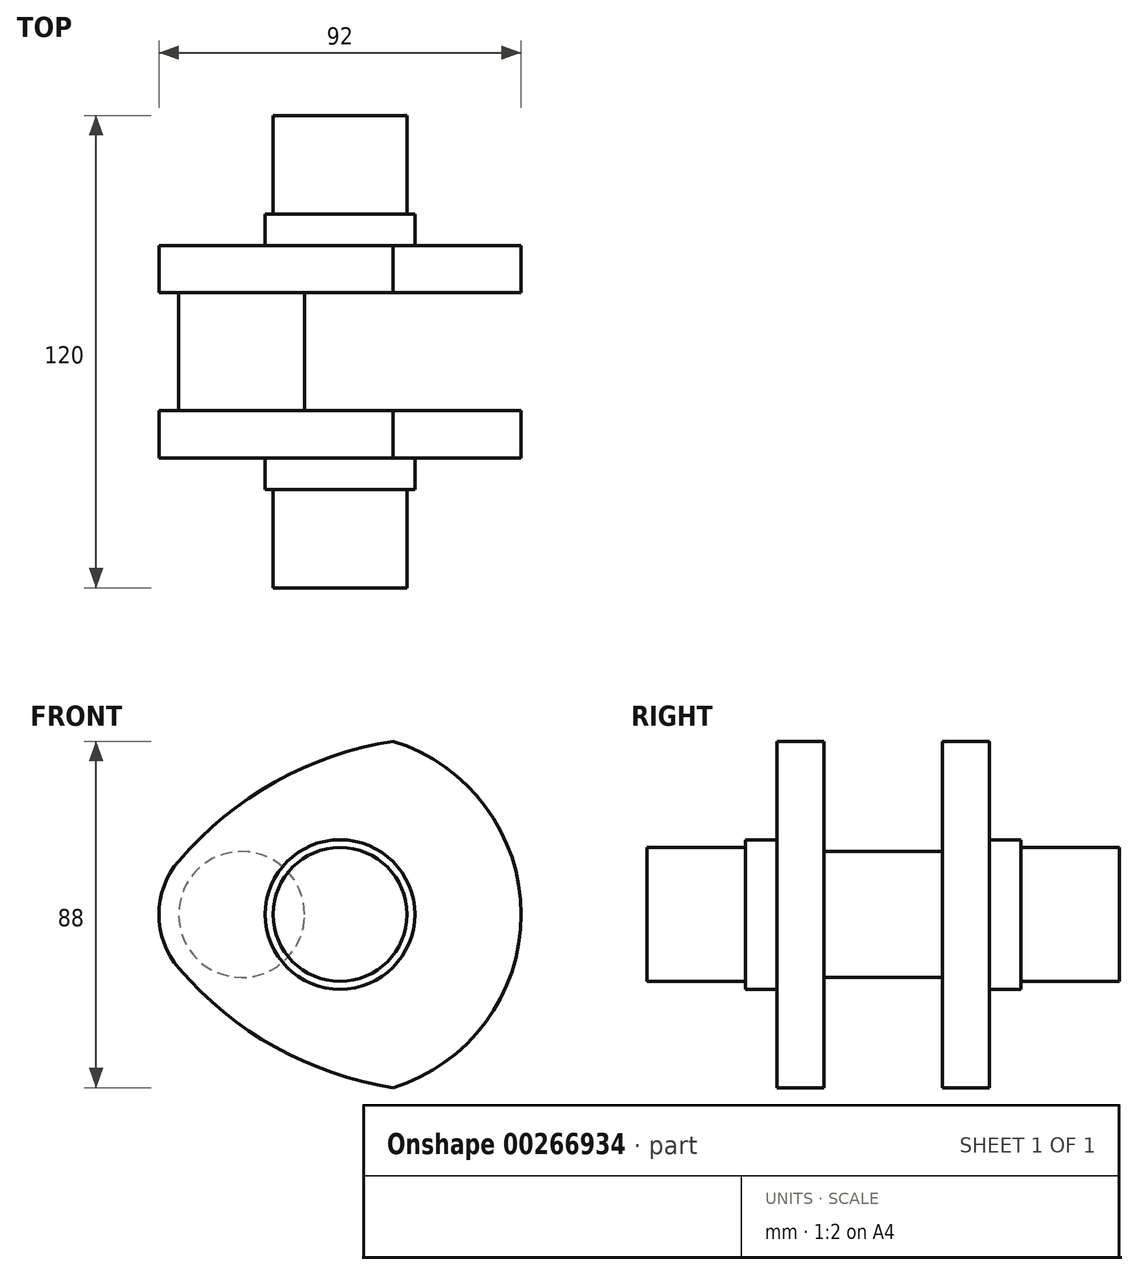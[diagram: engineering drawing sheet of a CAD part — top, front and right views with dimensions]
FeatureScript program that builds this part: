
annotation { "Feature Type Name" : "Feature", "Feature Type Description" : "" }
export const myFeature = defineFeature(function(context is Context, id is Id, definition is map)
    precondition{}
    {
        {
            var Q0;
            Q0=qCreatedBy(makeId("Front.planeOp"),FACE);
            var sketch = newSketch(context, id + "F0", { "sketchPlane" : qUnion([Q0])});
            skCircle(sketch, "E0", {"center": v(0, 0) * mm, "radius": 17 * mm});
            skSolve(sketch);
        }
        {
            var Q0;
            Q0=makeQuery(id+"F0.imprint","IMPRINT",FACE,{"disambiguationData":[TD([[makeQuery(id+"F0.imprint","IMPRINT",EDGE,{"derivedFrom":sQuery(id+"F0.wireOp",EDGE,"E0")}),1.0]])]});
            extrude(context, id + "F1", {"entities" : qUnion([Q0]), "depth" : 25 * mm});
        }
        {
            var Q0;
            Q0=makeQuery(id+"F0.imprint","IMPRINT",FACE,{"disambiguationData":[TD([[makeQuery(id+"F0.imprint","IMPRINT",EDGE,{"derivedFrom":sQuery(id+"F0.wireOp",EDGE,"E0")}),1.0]])]});
            var sketch = newSketch(context, id + "F2", { "sketchPlane" : qUnion([Q0])});
            skCircle(sketch, "E1", {"center": v(0, 0) * mm, "radius": 19 * mm});
            skSolve(sketch);
        }
        {
            var Q0;
            Q0 = qSketchRegion(id + "F2", true);
            extrude(context, id + "F3", {"entities" : qUnion([Q0]), "operationType" : NewBodyOperationType.ADD, "oppositeDirection" : true, "depth" : 8 * mm});
        }
        {
            var Q0;
            Q0=makeQuery(id+"F3.opExtrude","CAP_FACE",FACE,{"disambiguationData":[OSD([sQuery(id+"F2.wireOp",EDGE,"E1")])],"isStart":false});
            var sketch = newSketch(context, id + "F4", { "sketchPlane" : qUnion([Q0])});
            skArc(sketch, "E2", {"start": v(-13.42, 44) * mm, "mid": v(-46, 0) * mm, "end": v(-13.42, -44) * mm});
            skArc(sketch, "E3", {"start": v(40.94, -13.67) * mm, "mid": v(46, 0) * mm, "end": v(40.94, 13.67) * mm});
            skLineSegment(sketch, "E4", {"start": v(58.32, 0) * mm, "end": v(-25.77, 0) * mm, "construction": true});
            skArc(sketch, "E5", {"start": v(40.94, 13.67) * mm, "mid": v(16.47, 33.68) * mm, "end": v(-13.42, 44) * mm});
            skArc(sketch, "E6", {"start": v(-13.42, -44) * mm, "mid": v(16.47, -33.68) * mm, "end": v(40.94, -13.67) * mm});
            skSolve(sketch);
        }
        {
            var Q0;
            Q0=makeQuery(id+"F4.imprint","IMPRINT",FACE,{"disambiguationData":[TD([[makeQuery(id+"F4.imprint","IMPRINT",EDGE,{"derivedFrom":sQuery(id+"F4.wireOp",EDGE,"E2")}),1.0]])]});
            var Q1;
            Q1=makeQuery(id+"F4.imprint","IMPRINT",FACE,{"disambiguationData":[TD([[makeQuery(id+"F4.imprint","IMPRINT",EDGE,{"derivedFrom":makeQuery(id+"F3.opExtrude","CAP_EDGE",EDGE,{"disambiguationData":[OSD([sQuery(id+"F2.wireOp",EDGE,"E1")])],"isStart":false})}),-1.0]])]});
            extrude(context, id + "F5", {"entities" : qUnion([Q0, Q1]), "operationType" : NewBodyOperationType.ADD, "depth" : 12 * mm});
        }
        {
            var Q0;
            Q0=makeQuery(id+"F5.opExtrude","CAP_FACE",FACE,{"disambiguationData":[OSD([sQuery(id+"F4.wireOp",EDGE,"E2"),sQuery(id+"F4.wireOp",EDGE,"E3"),sQuery(id+"F4.wireOp",EDGE,"E5"),sQuery(id+"F4.wireOp",EDGE,"E6")])],"isStart":false});
            var sketch = newSketch(context, id + "F6", { "sketchPlane" : qUnion([Q0])});
            skCircle(sketch, "E7", {"center": v(25, 0) * mm, "radius": 16 * mm});
            skSolve(sketch);
        }
        {
            var Q0;
            Q0=makeQuery(id+"F6.imprint","IMPRINT",FACE,{"disambiguationData":[TD([[makeQuery(id+"F6.imprint","IMPRINT",EDGE,{"derivedFrom":sQuery(id+"F6.wireOp",EDGE,"E7")}),1.0]])]});
            extrude(context, id + "F7", {"entities" : qUnion([Q0]), "operationType" : NewBodyOperationType.ADD, "depth" : 15 * mm});
        }
        {
            var Q0;
            Q0=makeQuery(id+"F1.opExtrude","SWEPT_BODY",BODY,{"disambiguationData":[OSD([sQuery(id+"F0.wireOp",EDGE,"E0")])]});
            var Q1;
            Q1=makeQuery(id+"F7.opExtrude","CAP_FACE",FACE,{"disambiguationData":[OSD([sQuery(id+"F6.wireOp",EDGE,"E7")])],"isStart":false});
            mirror(context, id + "F8", {"operationType" : NewBodyOperationType.ADD, "entities" : qUnion([Q0]), "mirrorPlane" : qUnion([Q1])});
        }
    });
